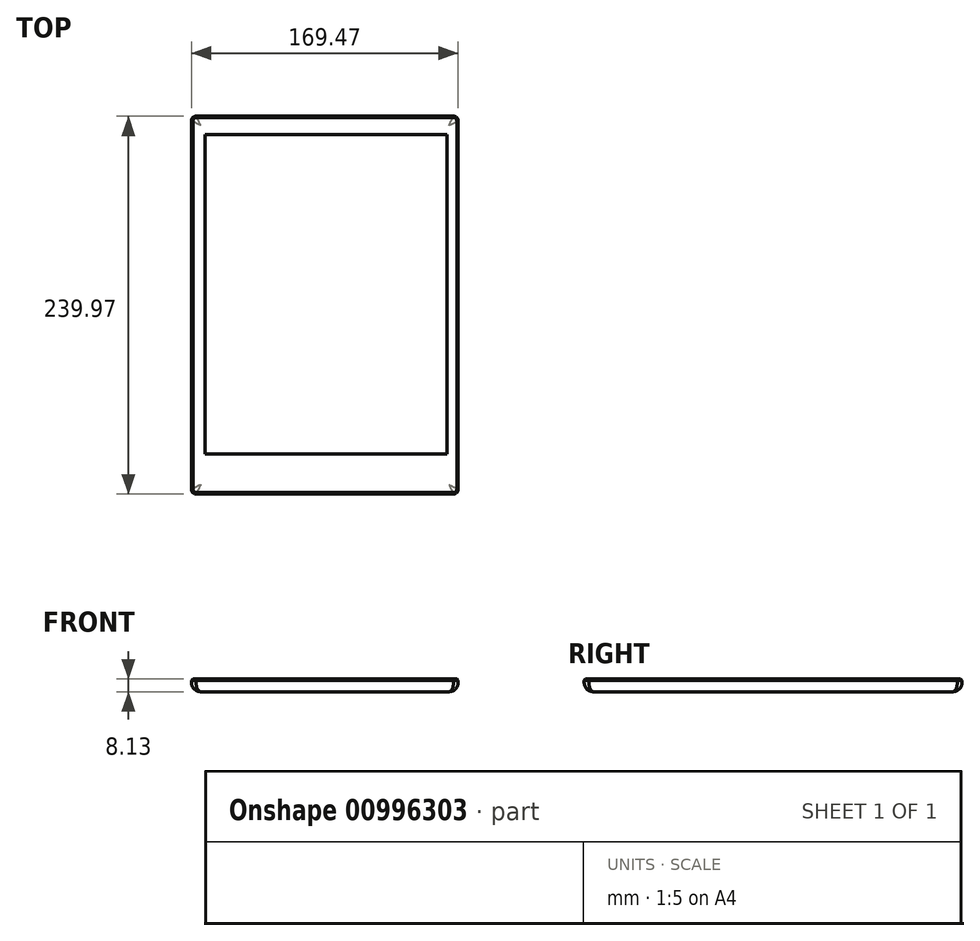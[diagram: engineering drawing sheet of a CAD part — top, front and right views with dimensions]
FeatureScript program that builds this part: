
annotation { "Feature Type Name" : "Feature", "Feature Type Description" : "" }
export const myFeature = defineFeature(function(context is Context, id is Id, definition is map)
    precondition{}
    {
        {
            var Q0;
            Q0=qCreatedBy(makeId("Top.planeOp"),FACE);
            var sketch = newSketch(context, id + "F0", { "sketchPlane" : qUnion([Q0])});
            skLineSegment(sketch, "E0.bottom", {"start": v(-87.43, 113.11) * mm, "end": v(76.05, 113.11) * mm});
            skLineSegment(sketch, "E0.top", {"start": v(-87.43, -126.86) * mm, "end": v(76.05, -126.86) * mm});
            skLineSegment(sketch, "E0.left", {"start": v(-90.42, 110.12) * mm, "end": v(-90.42, -123.87) * mm});
            skLineSegment(sketch, "E0.right", {"start": v(79.05, 110.12) * mm, "end": v(79.05, -123.87) * mm});
            skPoint(sketch, "E1.visualSharp", {"position": v(-90.42, 113.11) * mm});
            skArc(sketch, "E1.filletArc", {"start": v(-87.43, 113.11) * mm, "mid": v(-89.55, 112.24) * mm, "end": v(-90.42, 110.12) * mm});
            skPoint(sketch, "E2.visualSharp", {"position": v(79.05, 113.11) * mm});
            skArc(sketch, "E2.filletArc", {"start": v(79.05, 110.12) * mm, "mid": v(78.17, 112.24) * mm, "end": v(76.05, 113.11) * mm});
            skPoint(sketch, "E3.visualSharp", {"position": v(79.05, -126.86) * mm});
            skArc(sketch, "E3.filletArc", {"start": v(76.05, -126.86) * mm, "mid": v(78.17, -125.99) * mm, "end": v(79.05, -123.87) * mm});
            skPoint(sketch, "E4.visualSharp", {"position": v(-90.42, -126.86) * mm});
            skArc(sketch, "E4.filletArc", {"start": v(-90.42, -123.87) * mm, "mid": v(-89.55, -125.99) * mm, "end": v(-87.43, -126.86) * mm});
            skSolve(sketch);
        }
        {
            var Q0;
            Q0=makeQuery(id+"F0.imprint","IMPRINT",FACE,{"disambiguationData":[TD([[makeQuery(id+"F0.imprint","IMPRINT",EDGE,{"derivedFrom":sQuery(id+"F0.wireOp",EDGE,"E0.bottom")}),-1.0]])]});
            extrude(context, id + "F1", {"entities" : qUnion([Q0]), "depth" : 8.1 * mm, "offsetDistance" : 25.4 * mm});
        }
        {
            var Q0;
            Q0=makeQuery(id+"F1.opExtrude","CAP_FACE",FACE,{"disambiguationData":[OSD([sQuery(id+"F0.wireOp",EDGE,"E0.bottom"),sQuery(id+"F0.wireOp",EDGE,"E0.top"),sQuery(id+"F0.wireOp",EDGE,"E0.left"),sQuery(id+"F0.wireOp",EDGE,"E0.right"),sQuery(id+"F0.wireOp",EDGE,"E1.filletArc"),sQuery(id+"F0.wireOp",EDGE,"E2.filletArc"),sQuery(id+"F0.wireOp",EDGE,"E3.filletArc"),sQuery(id+"F0.wireOp",EDGE,"E4.filletArc")])],"isStart":true});
            fillet(context, id + "F2", {"entities" : qUnion([Q0]), "radius" : 5.9 * mm, "tangentPropagation" : true, "allowEdgeOverflow" : false});
        }
        {
            var Q0;
            Q0=makeQuery(id+"F1.opExtrude","CAP_FACE",FACE,{"disambiguationData":[OSD([sQuery(id+"F0.wireOp",EDGE,"E0.bottom"),sQuery(id+"F0.wireOp",EDGE,"E0.top"),sQuery(id+"F0.wireOp",EDGE,"E0.left"),sQuery(id+"F0.wireOp",EDGE,"E0.right"),sQuery(id+"F0.wireOp",EDGE,"E1.filletArc"),sQuery(id+"F0.wireOp",EDGE,"E2.filletArc"),sQuery(id+"F0.wireOp",EDGE,"E3.filletArc"),sQuery(id+"F0.wireOp",EDGE,"E4.filletArc")])],"isStart":false});
            chamfer(context, id + "F3", {"entities" : qUnion([Q0]), "width" : 0.94 * mm, "tangentPropagation" : true});
        }
        {
            var Q0;
            Q0=makeQuery(id+"F1.opExtrude","CAP_FACE",FACE,{"disambiguationData":[OSD([sQuery(id+"F0.wireOp",EDGE,"E0.bottom"),sQuery(id+"F0.wireOp",EDGE,"E0.top"),sQuery(id+"F0.wireOp",EDGE,"E0.left"),sQuery(id+"F0.wireOp",EDGE,"E0.right"),sQuery(id+"F0.wireOp",EDGE,"E1.filletArc"),sQuery(id+"F0.wireOp",EDGE,"E2.filletArc"),sQuery(id+"F0.wireOp",EDGE,"E3.filletArc"),sQuery(id+"F0.wireOp",EDGE,"E4.filletArc")])],"isStart":false});
            var sketch = newSketch(context, id + "F4", { "sketchPlane" : qUnion([Q0])});
            skLineSegment(sketch, "E5.bottom", {"start": v(-81.69, 101.54) * mm, "end": v(72.01, 101.54) * mm});
            skLineSegment(sketch, "E5.top", {"start": v(-81.69, -101.55) * mm, "end": v(72.01, -101.55) * mm});
            skLineSegment(sketch, "E5.left", {"start": v(-81.69, 101.54) * mm, "end": v(-81.69, -101.55) * mm});
            skLineSegment(sketch, "E5.right", {"start": v(72.01, 101.54) * mm, "end": v(72.01, -101.55) * mm});
            skSolve(sketch);
        }
        {
            var Q0;
            Q0=makeQuery(id+"F4.imprint","IMPRINT",FACE,{"disambiguationData":[TD([[makeQuery(id+"F4.imprint","IMPRINT",EDGE,{"derivedFrom":sQuery(id+"F4.wireOp",EDGE,"E5.bottom")}),-1.0]])]});
            extrude(context, id + "F5", {"entities" : qUnion([Q0]), "operationType" : NewBodyOperationType.ADD, "depth" : 0.03 * mm, "offsetDistance" : 25.4 * mm});
        }
    });
